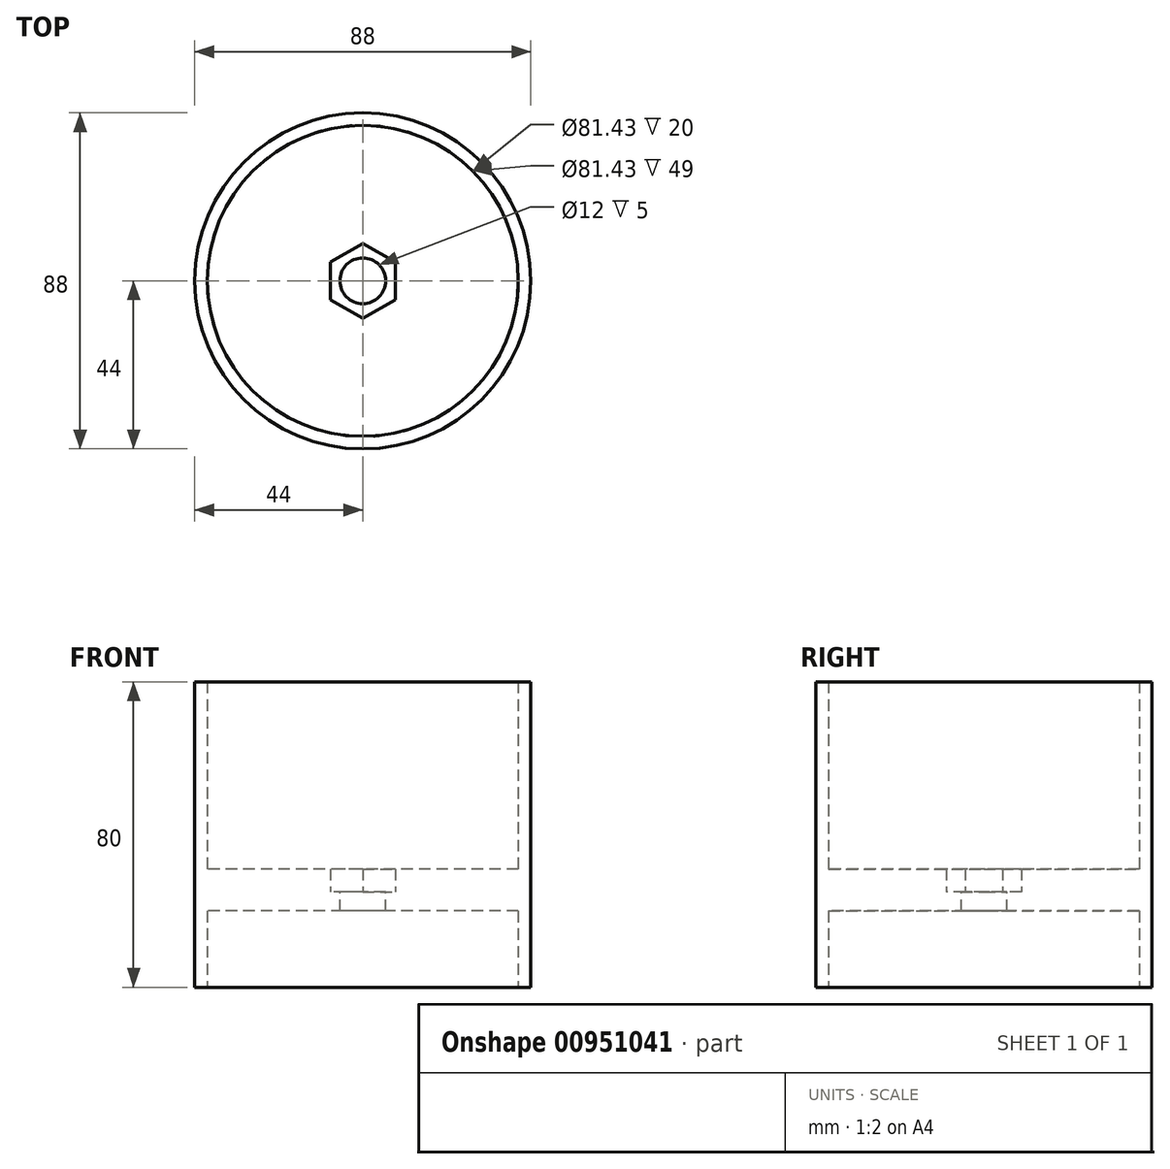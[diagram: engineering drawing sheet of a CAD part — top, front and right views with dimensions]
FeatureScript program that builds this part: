
annotation { "Feature Type Name" : "Feature", "Feature Type Description" : "" }
export const myFeature = defineFeature(function(context is Context, id is Id, definition is map)
    precondition{}
    {
        {
            var Q0;
            Q0=qCreatedBy(makeId("Top.planeOp"),FACE);
            var sketch = newSketch(context, id + "F0", { "sketchPlane" : qUnion([Q0])});
            skCircle(sketch, "E0", {"center": v(0, 0) * mm, "radius": 44 * mm});
            skCircle(sketch, "E1", {"center": v(0, 0) * mm, "radius": 40.71 * mm});
            skSolve(sketch);
        }
        {
            var Q0;
            Q0=makeQuery(id+"F0.imprint","IMPRINT",FACE,{"disambiguationData":[TD([[makeQuery(id+"F0.imprint","IMPRINT",EDGE,{"derivedFrom":sQuery(id+"F0.wireOp",EDGE,"E0")}),1.0]])]});
            extrude(context, id + "F1", {"entities" : qUnion([Q0]), "depth" : 80 * mm, "offsetDistance" : 25 * mm});
        }
        {
            var Q0;
            Q0=qCreatedBy(makeId("Top.planeOp"),FACE);
            cPlane(context, id + "F2", {"entities" : qUnion([Q0]), "cplaneType" : CPlaneType.OFFSET, "offset" : 25 * mm, "width" : 150 * mm, "height" : 150 * mm});
        }
        {
            var Q0;
            Q0=qCreatedBy(id+"F2.planeOp",FACE);
            var sketch = newSketch(context, id + "F3", { "sketchPlane" : qUnion([Q0])});
            skCircle(sketch, "E2.cCircle", {"center": v(0, 0) * mm, "radius": 8.5 * mm, "construction": true});
            skLineSegment(sketch, "E2.0", {"start": v(8.5, 4.9) * mm, "end": v(8.5, -4.9) * mm});
            skLineSegment(sketch, "E2.1", {"start": v(8.5, -4.9) * mm, "end": v(0, -9.81) * mm});
            skLineSegment(sketch, "E2.2", {"start": v(0, -9.81) * mm, "end": v(-8.5, -4.9) * mm});
            skLineSegment(sketch, "E2.3", {"start": v(-8.5, -4.9) * mm, "end": v(-8.5, 4.9) * mm});
            skLineSegment(sketch, "E2.4", {"start": v(-8.5, 4.9) * mm, "end": v(0, 9.81) * mm});
            skLineSegment(sketch, "E2.5", {"start": v(0, 9.81) * mm, "end": v(8.5, 4.9) * mm});
            skPoint(sketch, "E2.0.midPoint", {"position": v(8.5, 0) * mm});
            skCircle(sketch, "E3", {"center": v(0, 0) * mm, "radius": 40.71 * mm});
            skSolve(sketch);
        }
        {
            var Q0;
            Q0 = qSketchRegion(id + "F3", true);
            var Q1;
            Q1=makeQuery(id+"F3.imprint","IMPRINT",FACE,{"disambiguationData":[TD([[makeQuery(id+"F3.imprint","IMPRINT",EDGE,{"derivedFrom":sQuery(id+"F3.wireOp",EDGE,"E2.0")}),-1.0]])]});
            extrude(context, id + "F4", {"entities" : qUnion([Q0, Q1]), "operationType" : NewBodyOperationType.ADD, "oppositeDirection" : true, "depth" : 5 * mm, "offsetDistance" : 25 * mm});
        }
        {
            var Q0;
            Q0=makeQuery(id+"F3.imprint","IMPRINT",FACE,{"disambiguationData":[TD([[makeQuery(id+"F3.imprint","IMPRINT",EDGE,{"derivedFrom":sQuery(id+"F3.wireOp",EDGE,"E2.0")}),1.0]])]});
            extrude(context, id + "F5", {"entities" : qUnion([Q0]), "operationType" : NewBodyOperationType.ADD, "depth" : 6 * mm, "offsetDistance" : 25 * mm});
        }
        {
            var Q0;
            Q0=sQuery(id+"F3.wireOp",VERTEX,"E2.cCircle.center");
            var Q1;
            Q1=makeQuery(id+"F1.opExtrude","SWEPT_BODY",BODY,{"disambiguationData":[OSD([sQuery(id+"F0.wireOp",EDGE,"E0"),sQuery(id+"F0.wireOp",EDGE,"E1")])]});
            hole(context, id + "F6", {"style" : HoleStyle.SIMPLE, "endStyle" : HoleEndStyle.THROUGH, "holeDiameter" : 12 * mm, "majorDiameter" : 5 * mm, "isTappedThrough" : true, "tappedDepth" : 12 * mm, "tapClearance" : 3, "startFromSketch" : true, "locations" : qUnion([Q0]), "scope" : qUnion([Q1])});
        }
    });
